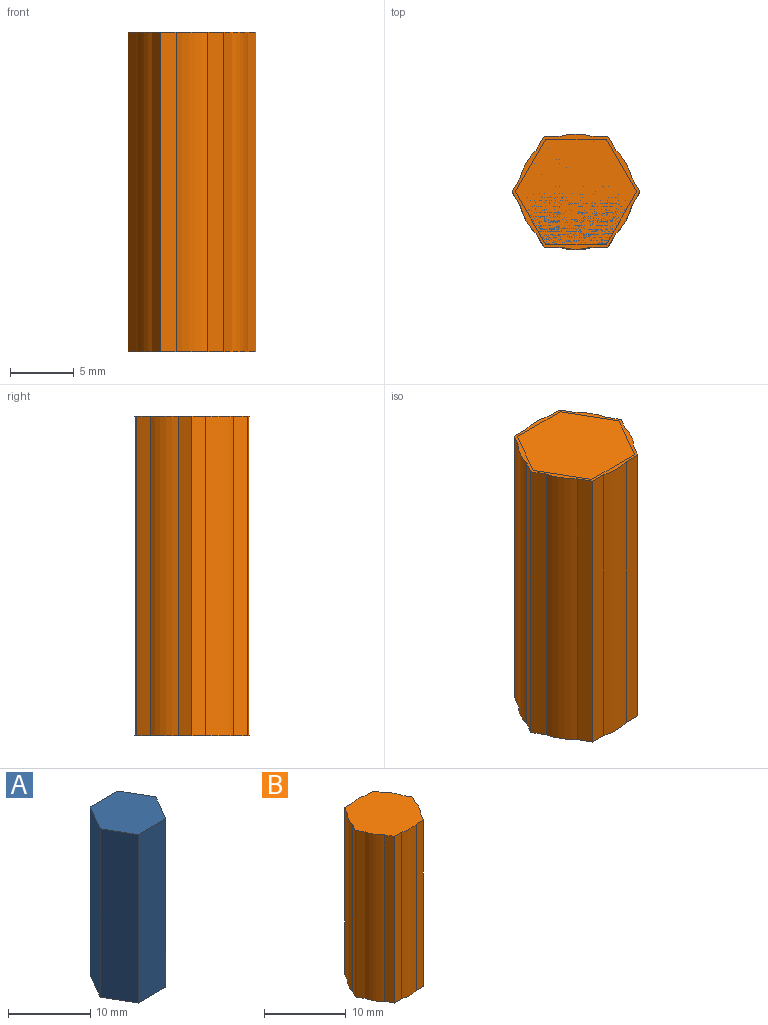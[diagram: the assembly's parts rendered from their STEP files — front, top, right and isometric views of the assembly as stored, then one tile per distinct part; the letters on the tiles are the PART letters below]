
ASSEMBLY  parts=2 mates=1
PART A: 8 faces, bbox 9.5x8.2x25 mm
  f0: plane 25x4.11mm, normal (-0.87,-0.5,0), area 118.8mm2, adj f1,f5,f6,f7
  f1: plane 25x4.75mm, normal (0,-1,0), area 118.8mm2, adj f0,f2,f6,f7
  f2: plane 25x4.11mm, normal (0.87,-0.5,0), area 118.8mm2, adj f1,f3,f6,f7
  f3: plane 25x4.11mm, normal (0.87,0.5,0), area 118.8mm2, adj f2,f4,f6,f7
  f4: plane 25x4.75mm, normal (0,1,0), area 118.8mm2, adj f3,f5,f6,f7
  f5: plane 25x4.11mm, normal (-0.87,0.5,0), area 118.8mm2, adj f0,f4,f6,f7
  f6: plane 9.5x8.23mm, normal (0,0,1), area 58.6mm2, adj f0,f1,f2,f3,f4,f5
  f7: plane 9.5x8.23mm, normal (0,0,-1), area 58.6mm2, adj f0,f1,f2,f3,f4,f5
PART B: 20 faces, bbox 10x9x25 mm
  f0: cylinder r=4.51mm len=25mm, axis (0,0,-1), area 63.3mm2, adj f1,f17,f18,f19
  f1: plane 25x1.08mm, normal (0.87,-0.5,0), area 31.3mm2, adj f0,f2,f18,f19
  f2: plane 25x1.08mm, normal (0.87,0.5,0), area 31.3mm2, adj f1,f3,f18,f19
  f3: cylinder r=4.51mm len=25mm, axis (0,0,-1), area 63.3mm2, adj f2,f4,f18,f19
  f4: plane 25x1.08mm, normal (0.87,0.5,0), area 31.3mm2, adj f3,f5,f18,f19
  f5: plane 25x1.25mm, normal (0,1,0), area 31.2mm2, adj f4,f6,f18,f19
  f6: cylinder r=4.51mm len=25mm, axis (0,0,-1), area 63.3mm2, adj f5,f7,f18,f19
  f7: plane 25x1.25mm, normal (0,1,0), area 31.2mm2, adj f6,f8,f18,f19
  f8: plane 25x1.08mm, normal (-0.87,0.5,0), area 31.3mm2, adj f7,f9,f18,f19
  f9: cylinder r=4.51mm len=25mm, axis (0,0,-1), area 63.3mm2, adj f8,f10,f18,f19
  f10: plane 25x1.08mm, normal (-0.87,0.5,0), area 31.3mm2, adj f9,f11,f18,f19
  f11: plane 25x1.08mm, normal (-0.87,-0.5,0), area 31.3mm2, adj f10,f12,f18,f19
  f12: cylinder r=4.51mm len=25mm, axis (0,0,-1), area 63.3mm2, adj f11,f13,f18,f19
  f13: plane 25x1.08mm, normal (-0.87,-0.5,0), area 31.3mm2, adj f12,f14,f18,f19
  f14: plane 25x1.25mm, normal (0,-1,0), area 31.2mm2, adj f13,f15,f18,f19
  f15: cylinder r=4.51mm len=25mm, axis (0,0,-1), area 63.3mm2, adj f14,f16,f18,f19
  f16: plane 25x1.25mm, normal (0,-1,0), area 31.2mm2, adj f15,f17,f18,f19
  f17: plane 25x1.08mm, normal (0.87,-0.5,0), area 31.3mm2, adj f0,f16,f18,f19
  f18: plane 10x9.01mm, normal (0,0,1), area 66.7mm2, adj f0,f1,f2,f3,f4,f5,f6,f7
  f19: plane 10x9.01mm, normal (0,0,-1), area 66.7mm2, adj f0,f1,f2,f3,f4,f5,f6,f7
PLACE A at identity
PLACE B at identity
MATE fastened A.f6 <-> B.f15  axis (0,0,1) through (0,0,25)mm
